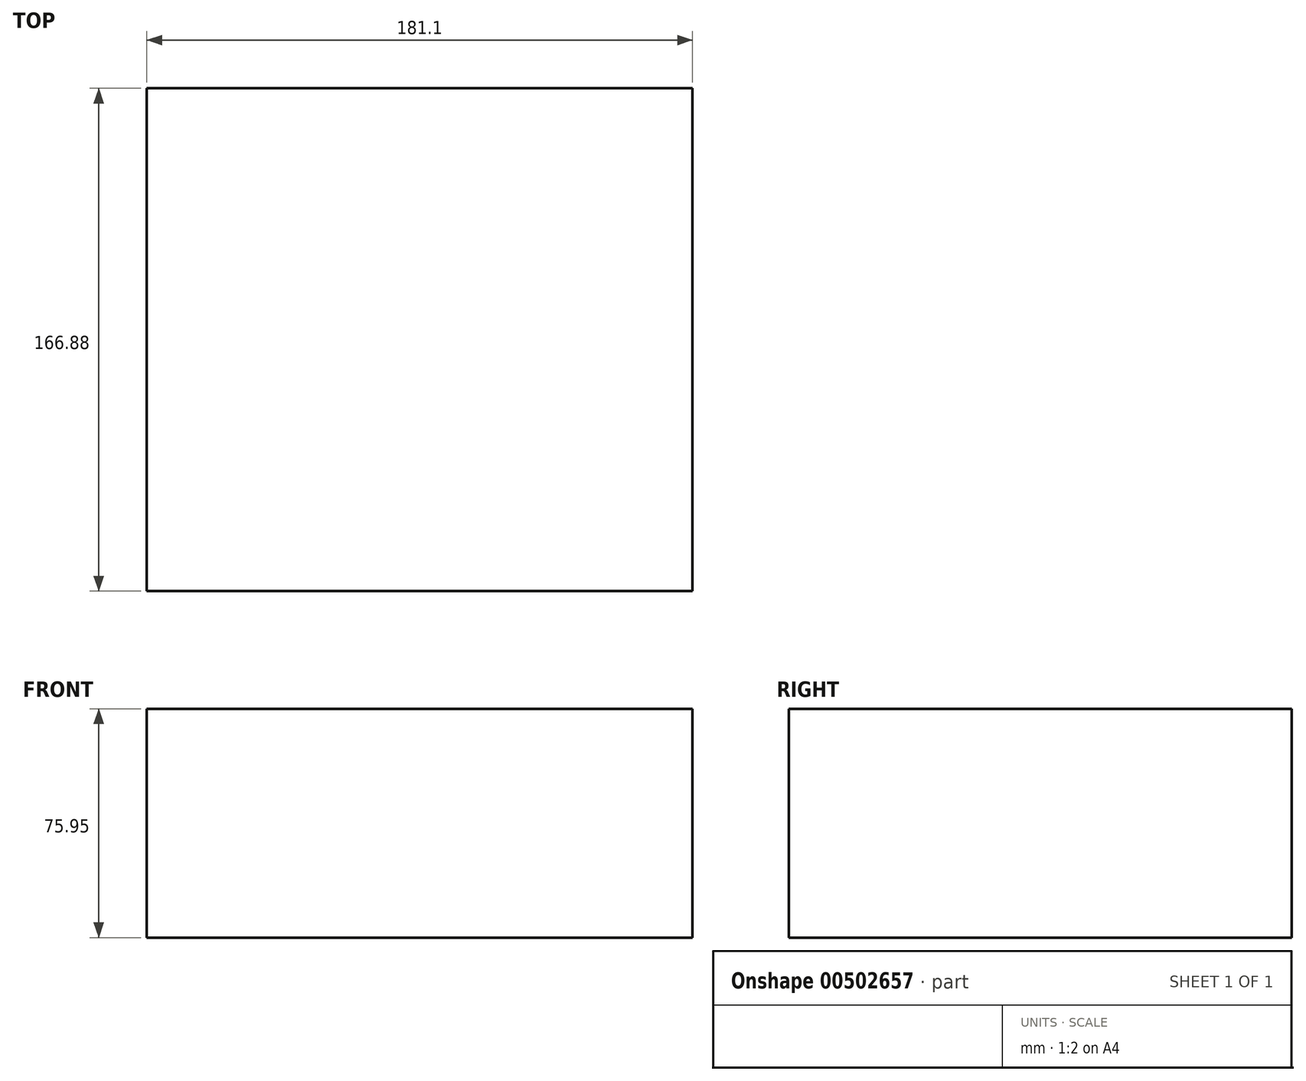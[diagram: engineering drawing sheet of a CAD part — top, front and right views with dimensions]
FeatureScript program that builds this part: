
annotation { "Feature Type Name" : "Feature", "Feature Type Description" : "" }
export const myFeature = defineFeature(function(context is Context, id is Id, definition is map)
    precondition{}
    {
        {
            var Q0;
            Q0=qCreatedBy(makeId("Front.planeOp"),FACE);
            var sketch = newSketch(context, id + "F0", { "sketchPlane" : qUnion([Q0])});
            skLineSegment(sketch, "E0.bottom", {"start": v(0, 0) * mm, "end": v(-181.1, 0) * mm});
            skLineSegment(sketch, "E0.top", {"start": v(0, 75.95) * mm, "end": v(-181.1, 75.95) * mm});
            skLineSegment(sketch, "E0.left", {"start": v(0, 0) * mm, "end": v(0, 75.95) * mm});
            skLineSegment(sketch, "E0.right", {"start": v(-181.1, 0) * mm, "end": v(-181.1, 75.95) * mm});
            skSolve(sketch);
        }
        {
            var Q0;
            Q0=qSketchRegion(id+"F0",true);
            extrude(context, id + "F1", {"entities" : qUnion([Q0]), "depth" : 166.88 * mm});
        }
    });
